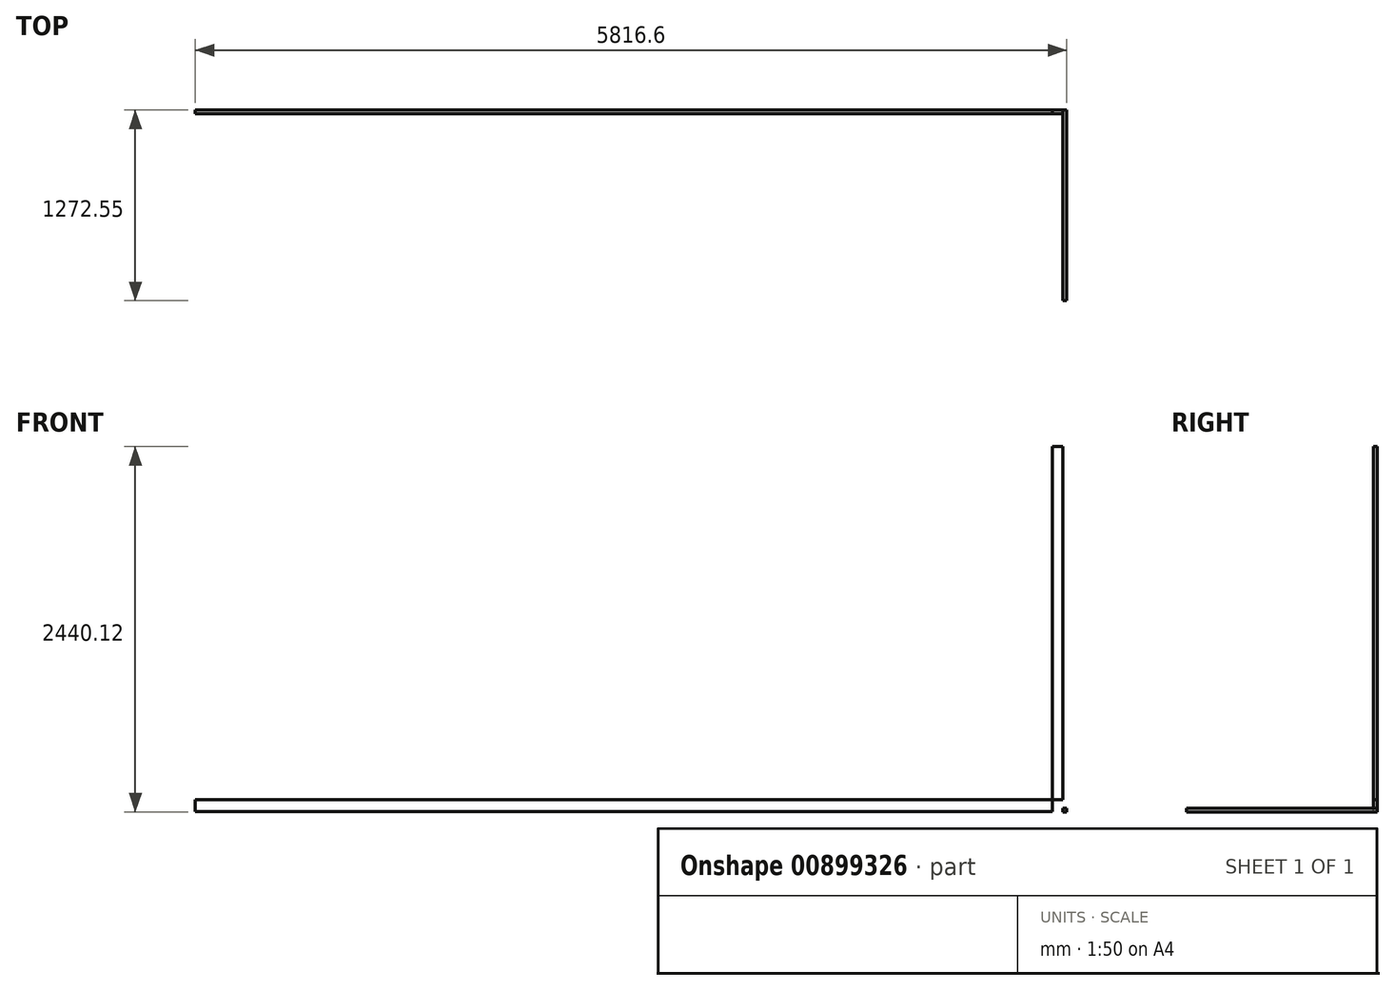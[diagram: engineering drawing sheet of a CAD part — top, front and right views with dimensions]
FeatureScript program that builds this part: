
annotation { "Feature Type Name" : "Feature", "Feature Type Description" : "" }
export const myFeature = defineFeature(function(context is Context, id is Id, definition is map)
    precondition{}
    {
        {
            var Q0;
            Q0=qCreatedBy(makeId("Front.planeOp"),FACE);
            var sketch = newSketch(context, id + "F0", { "sketchPlane" : qUnion([Q0])});
            skLineSegment(sketch, "E0.bottom", {"start": v(-71, -1269.38) * mm, "end": v(0, -1269.38) * mm});
            skLineSegment(sketch, "E0.top", {"start": v(-71, 1169.02) * mm, "end": v(0, 1169.02) * mm});
            skLineSegment(sketch, "E0.left", {"start": v(0, -1269.38) * mm, "end": v(0, 1169.02) * mm});
            skLineSegment(sketch, "E0.right", {"start": v(-71, -1269.38) * mm, "end": v(-71, 1169.02) * mm});
            skLineSegment(sketch, "E1.bottom", {"start": v(0, -1269.38) * mm, "end": v(-5791.2, -1269.38) * mm});
            skLineSegment(sketch, "E1.top", {"start": v(0, -1188.16) * mm, "end": v(-5791.2, -1188.16) * mm});
            skLineSegment(sketch, "E1.left", {"start": v(0, -1269.38) * mm, "end": v(0, -1188.16) * mm});
            skLineSegment(sketch, "E1.right", {"start": v(-5791.2, -1269.38) * mm, "end": v(-5791.2, -1188.16) * mm});
            skSolve(sketch);
        }
        {
            var Q0;
            {var subQ0=sQuery(id+"F0.wireOp",EDGE,"E0.top");Q0=makeQuery(id+"F0.imprint","IMPRINT",FACE,{"disambiguationData":[TD([[makeQuery(id+"F0.imprint","IMPRINT",EDGE,{"derivedFrom":subQ0}),-1.0]])]});}
            extrude(context, id + "F1", {"entities" : qUnion([Q0]), "depth" : 25.4 * mm, "offsetDistance" : 25.4 * mm});
        }
        {
            var Q0;
            {var subQ5=sQuery(id+"F0.wireOp",EDGE,"E1.right");Q0=makeQuery(id+"F0.imprint","IMPRINT",FACE,{"disambiguationData":[TD([[makeQuery(id+"F0.imprint","IMPRINT",EDGE,{"derivedFrom":subQ5}),-1.0]])]});}
            extrude(context, id + "F2", {"entities" : qUnion([Q0]), "depth" : 25.4 * mm, "offsetDistance" : 25.4 * mm});
        }
        {
            var Q0;
            Q0=qCreatedBy(makeId("Right.planeOp"),FACE);
            var sketch = newSketch(context, id + "F3", { "sketchPlane" : qUnion([Q0])});
            skLineSegment(sketch, "E2.bottom", {"start": v(0, -1271.1) * mm, "end": v(-1272.55, -1271.1) * mm});
            skLineSegment(sketch, "E2.top", {"start": v(0, -1245.81) * mm, "end": v(-1272.55, -1245.81) * mm});
            skLineSegment(sketch, "E2.left", {"start": v(0, -1271.1) * mm, "end": v(0, -1245.81) * mm});
            skLineSegment(sketch, "E2.right", {"start": v(-1272.55, -1271.1) * mm, "end": v(-1272.55, -1245.81) * mm});
            skSolve(sketch);
        }
        {
            var Q0;
            Q0 = qSketchRegion(id + "F3", true);
            extrude(context, id + "F4", {"entities" : qUnion([Q0]), "depth" : 25.4 * mm, "offsetDistance" : 25.4 * mm});
        }
    });
